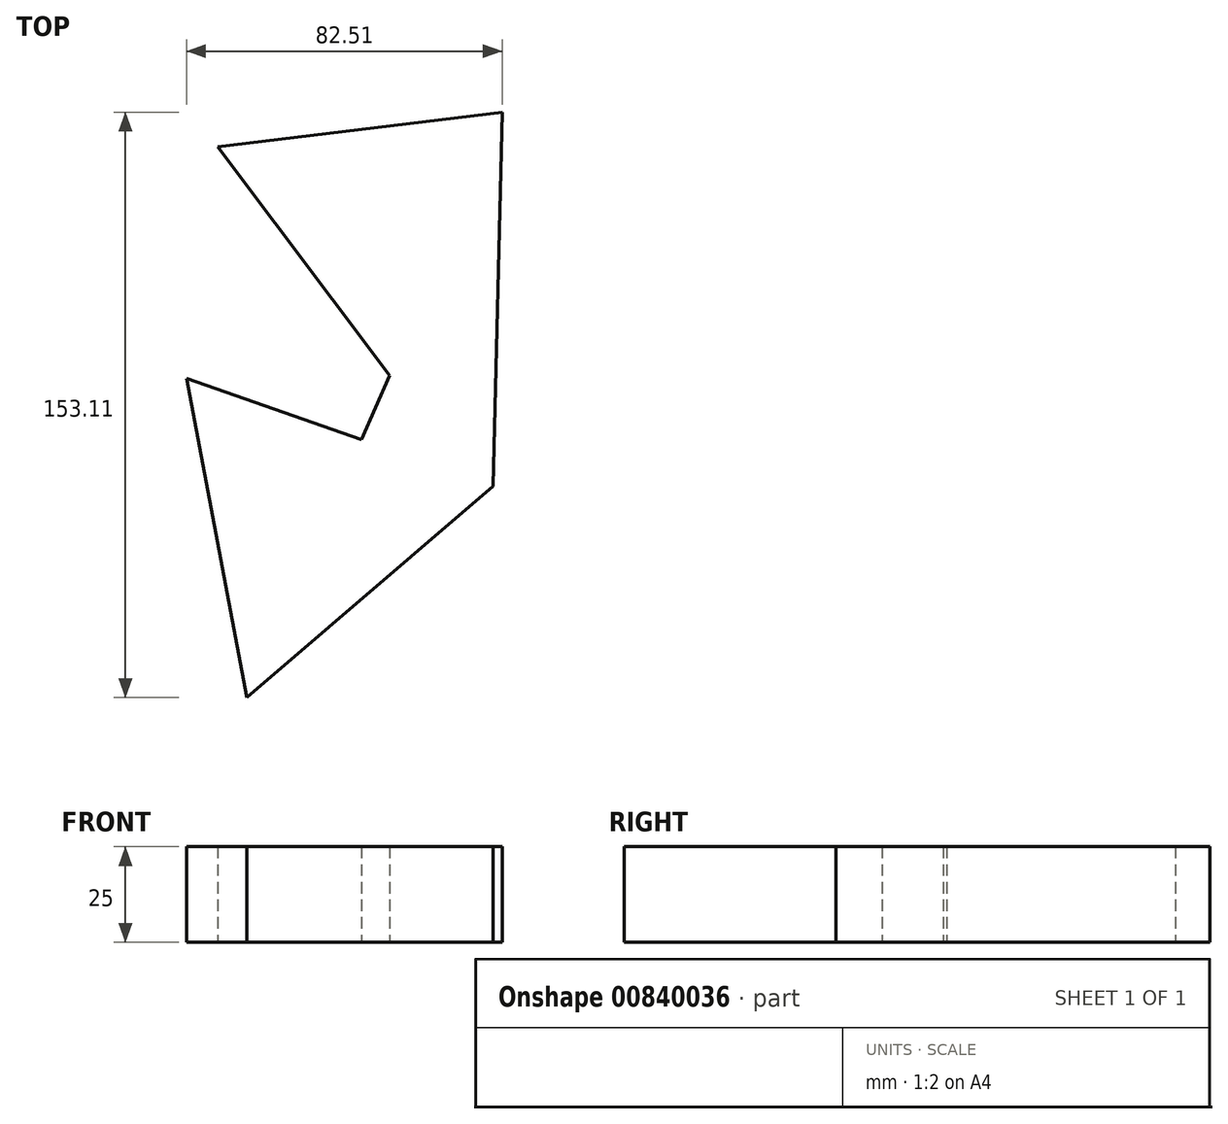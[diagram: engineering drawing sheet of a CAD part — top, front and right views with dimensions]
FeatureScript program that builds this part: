
annotation { "Feature Type Name" : "Feature", "Feature Type Description" : "" }
export const myFeature = defineFeature(function(context is Context, id is Id, definition is map)
    precondition{}
    {
        {
            var Q0;
            Q0=qCreatedBy(makeId("Top.planeOp"),FACE);
            var sketch = newSketch(context, id + "F0", { "sketchPlane" : qUnion([Q0])});
            skCircle(sketch, "E0.cCircle", {"center": v(-12.55, 40.76) * mm, "radius": 21.62 * mm, "construction": true});
            skLineSegment(sketch, "E0.0", {"start": v(22.02, 66.74) * mm, "end": v(-7.35, -2.17) * mm});
            skLineSegment(sketch, "E0.1", {"start": v(-7.35, -2.17) * mm, "end": v(-52.34, 57.72) * mm});
            skLineSegment(sketch, "E0.2", {"start": v(-52.34, 57.72) * mm, "end": v(22.02, 66.74) * mm});
            skPoint(sketch, "E0.0.midPoint", {"position": v(7.34, 32.28) * mm});
            skCircle(sketch, "E1.cCircle", {"center": v(-28.53, -40.1) * mm, "radius": 24.51 * mm, "construction": true});
            skLineSegment(sketch, "E1.0", {"start": v(19.64, -31.02) * mm, "end": v(-44.75, -86.37) * mm});
            skLineSegment(sketch, "E1.1", {"start": v(-44.75, -86.37) * mm, "end": v(-60.49, -2.93) * mm});
            skLineSegment(sketch, "E1.2", {"start": v(-60.49, -2.93) * mm, "end": v(19.64, -31.02) * mm});
            skPoint(sketch, "E1.0.midPoint", {"position": v(-12.55, -58.7) * mm});
            skLineSegment(sketch, "E2", {"start": v(-55.27, 57.72) * mm, "end": v(-60.49, -2.93) * mm});
            skLineSegment(sketch, "E3", {"start": v(-7.35, -2.17) * mm, "end": v(-44.75, -86.37) * mm});
            skLineSegment(sketch, "E4", {"start": v(22.02, 66.74) * mm, "end": v(19.64, -31.02) * mm});
            skSolve(sketch);
        }
        {
            var Q0;
            Q0 = qSketchRegion(id + "F0", true);
            extrude(context, id + "F1", {"entities" : qUnion([Q0]), "depth" : 25 * mm, "offsetDistance" : 25 * mm});
        }
    });
